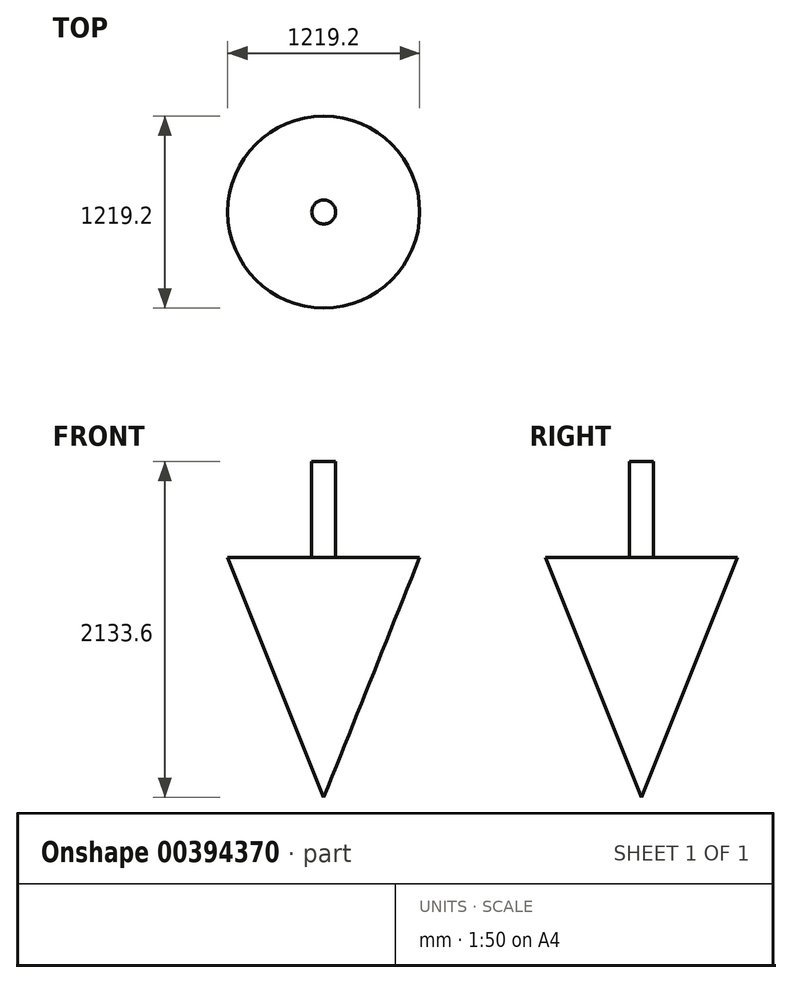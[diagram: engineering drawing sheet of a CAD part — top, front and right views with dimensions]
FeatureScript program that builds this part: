
annotation { "Feature Type Name" : "Feature", "Feature Type Description" : "" }
export const myFeature = defineFeature(function(context is Context, id is Id, definition is map)
    precondition{}
    {
        {
            var Q0;
            Q0=qCreatedBy(makeId("Top.planeOp"),FACE);
            var sketch = newSketch(context, id + "F0", { "sketchPlane" : qUnion([Q0])});
            skCircle(sketch, "E0", {"center": v(0, 0) * mm, "radius": 609.6 * mm});
            skSolve(sketch);
        }
        {
            var Q0;
            Q0=qCreatedBy(makeId("Top.planeOp"),FACE);
            cPlane(context, id + "F1", {"entities" : qUnion([Q0]), "cplaneType" : CPlaneType.OFFSET, "offset" : 609.6 * mm, "width" : 152.4 * mm, "height" : 152.4 * mm});
        }
        {
            var Q0;
            Q0=qCreatedBy(id+"F1.planeOp",FACE);
            var sketch = newSketch(context, id + "F2", { "sketchPlane" : qUnion([Q0])});
            skCircle(sketch, "E1", {"center": v(0, 0) * mm, "radius": 76.2 * mm});
            skSolve(sketch);
        }
        {
            var Q0;
            Q0 = qSketchRegion(id + "F2", true);
            extrude(context, id + "F3", {"entities" : qUnion([Q0]), "oppositeDirection" : true, "depth" : 609.6 * mm});
        }
        {
            var Q0;
            Q0=makeQuery(id+"F0.imprint","IMPRINT",FACE,{"disambiguationData":[TD([[makeQuery(id+"F0.imprint","IMPRINT",EDGE,{"derivedFrom":sQuery(id+"F0.wireOp",EDGE,"E0")}),1.0]])]});
            cPlane(context, id + "F4", {"entities" : qUnion([Q0]), "cplaneType" : CPlaneType.OFFSET, "offset" : 1524 * mm, "oppositeDirection" : true, "width" : 152.4 * mm, "height" : 152.4 * mm});
        }
        {
            var Q0;
            Q0=qCreatedBy(id+"F4.planeOp",FACE);
            var sketch = newSketch(context, id + "F5", { "sketchPlane" : qUnion([Q0])});
            skPoint(sketch, "E2", {"position": v(0, 0) * mm});
            skSolve(sketch);
        }
        {
            var Q1;
            Q1=makeQuery(id+"F0.imprint","IMPRINT",FACE,{"disambiguationData":[TD([[makeQuery(id+"F0.imprint","IMPRINT",EDGE,{"derivedFrom":sQuery(id+"F0.wireOp",EDGE,"E0")}),1.0]])]});
            var Q2;
            Q2=sQuery(id+"F5.wireOp",VERTEX,"E2");
            loft(context, id + "F6", {"operationType" : NewBodyOperationType.ADD, "sheetProfilesArray" : [{ "sheetProfileEntities" : qUnion([Q1]) }, { "sheetProfileEntities" : qUnion([Q2]) }]});
        }
    });
